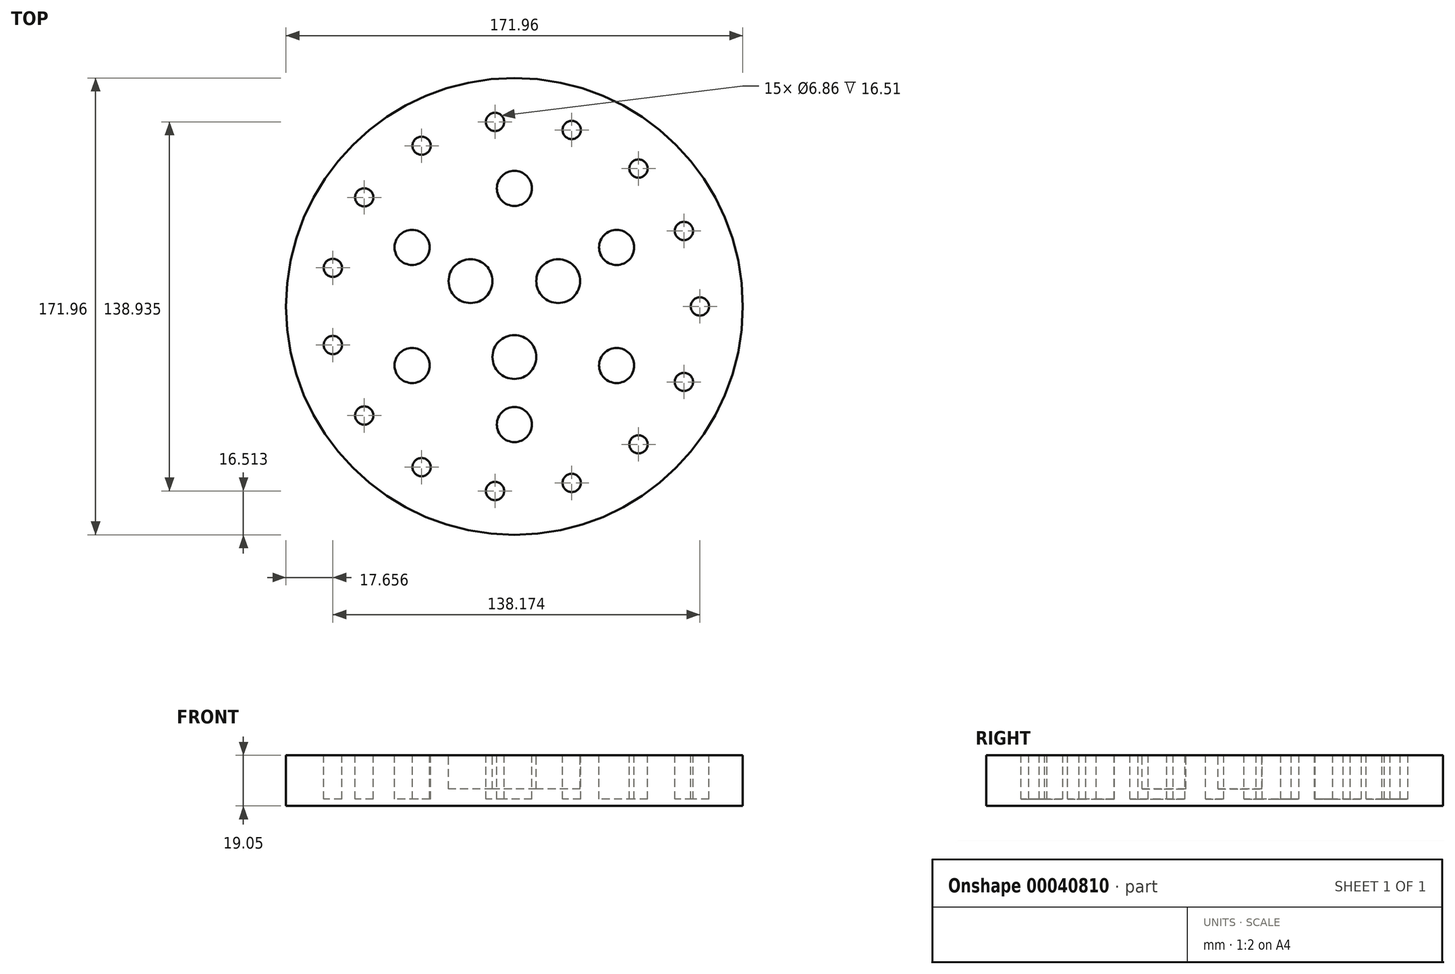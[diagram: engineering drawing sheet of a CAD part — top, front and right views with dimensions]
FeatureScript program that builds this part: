
annotation { "Feature Type Name" : "Feature", "Feature Type Description" : "" }
export const myFeature = defineFeature(function(context is Context, id is Id, definition is map)
    precondition{}
    {
        {
            var Q0;
            Q0=qCreatedBy(makeId("Top.planeOp"),FACE);
            var sketch = newSketch(context, id + "F0", { "sketchPlane" : qUnion([Q0])});
            skCircle(sketch, "E0", {"center": v(0, -19.05) * mm, "radius": 8.26 * mm});
            skCircle(sketch, "E1.1.0", {"center": v(16.5, 9.52) * mm, "radius": 8.26 * mm});
            skCircle(sketch, "E1.2.0", {"center": v(-16.5, 9.52) * mm, "radius": 8.26 * mm});
            skPoint(sketch, "E1.center", {"position": v(0, 0) * mm});
            skCircle(sketch, "E2", {"center": v(0, 44.45) * mm, "radius": 6.6 * mm});
            skCircle(sketch, "E3.1.0", {"center": v(-38.5, 22.23) * mm, "radius": 6.6 * mm});
            skCircle(sketch, "E3.2.0", {"center": v(-38.5, -22.23) * mm, "radius": 6.6 * mm});
            skCircle(sketch, "E4.1.3.0", {"center": v(0, -44.45) * mm, "radius": 6.6 * mm});
            skCircle(sketch, "E4.1.4.0", {"center": v(38.5, -22.23) * mm, "radius": 6.6 * mm});
            skCircle(sketch, "E4.1.5.0", {"center": v(38.5, 22.23) * mm, "radius": 6.6 * mm});
            skCircle(sketch, "E5", {"center": v(69.85, 0) * mm, "radius": 3.43 * mm});
            skCircle(sketch, "E6.1.0", {"center": v(63.81, 28.41) * mm, "radius": 3.43 * mm});
            skCircle(sketch, "E6.2.0", {"center": v(46.74, 51.9) * mm, "radius": 3.43 * mm});
            skCircle(sketch, "E6.3.0", {"center": v(21.58, 66.43) * mm, "radius": 3.43 * mm});
            skCircle(sketch, "E6.4.0", {"center": v(-7.3, 69.47) * mm, "radius": 3.43 * mm});
            skCircle(sketch, "E6.5.0", {"center": v(-34.92, 60.5) * mm, "radius": 3.43 * mm});
            skCircle(sketch, "E6.6.0", {"center": v(-56.5, 41.06) * mm, "radius": 3.43 * mm});
            skCircle(sketch, "E6.7.0", {"center": v(-68.32, 14.52) * mm, "radius": 3.43 * mm});
            skCircle(sketch, "E6.8.0", {"center": v(-68.32, -14.52) * mm, "radius": 3.43 * mm});
            skCircle(sketch, "E6.9.0", {"center": v(-56.5, -41.06) * mm, "radius": 3.43 * mm});
            skCircle(sketch, "E6.10.0", {"center": v(-34.93, -60.5) * mm, "radius": 3.43 * mm});
            skCircle(sketch, "E6.11.0", {"center": v(-7.3, -69.47) * mm, "radius": 3.43 * mm});
            skCircle(sketch, "E6.12.0", {"center": v(21.58, -66.43) * mm, "radius": 3.43 * mm});
            skCircle(sketch, "E6.13.0", {"center": v(46.74, -51.9) * mm, "radius": 3.43 * mm});
            skCircle(sketch, "E6.14.0", {"center": v(63.81, -28.41) * mm, "radius": 3.43 * mm});
            skCircle(sketch, "E7", {"center": v(0, 0) * mm, "radius": 85.98 * mm});
            skSolve(sketch);
        }
        {
            var Q0;
            Q0=makeQuery(id+"F0.imprint","IMPRINT",FACE,{"disambiguationData":[TD([[makeQuery(id+"F0.imprint","IMPRINT",EDGE,{"derivedFrom":sQuery(id+"F0.wireOp",EDGE,"E0")}),-1.0]])]});
            var Q1;
            Q1=makeQuery(id+"F0.imprint","IMPRINT",FACE,{"disambiguationData":[TD([[makeQuery(id+"F0.imprint","IMPRINT",EDGE,{"derivedFrom":sQuery(id+"F0.wireOp",EDGE,"E6.7.0")}),1.0]])]});
            var Q2;
            Q2=makeQuery(id+"F0.imprint","IMPRINT",FACE,{"disambiguationData":[TD([[makeQuery(id+"F0.imprint","IMPRINT",EDGE,{"derivedFrom":sQuery(id+"F0.wireOp",EDGE,"E6.8.0")}),1.0]])]});
            var Q3;
            Q3=makeQuery(id+"F0.imprint","IMPRINT",FACE,{"disambiguationData":[TD([[makeQuery(id+"F0.imprint","IMPRINT",EDGE,{"derivedFrom":sQuery(id+"F0.wireOp",EDGE,"E6.9.0")}),1.0]])]});
            var Q4;
            Q4=makeQuery(id+"F0.imprint","IMPRINT",FACE,{"disambiguationData":[TD([[makeQuery(id+"F0.imprint","IMPRINT",EDGE,{"derivedFrom":sQuery(id+"F0.wireOp",EDGE,"E6.10.0")}),1.0]])]});
            var Q5;
            Q5=makeQuery(id+"F0.imprint","IMPRINT",FACE,{"disambiguationData":[TD([[makeQuery(id+"F0.imprint","IMPRINT",EDGE,{"derivedFrom":sQuery(id+"F0.wireOp",EDGE,"E6.11.0")}),1.0]])]});
            var Q6;
            Q6=makeQuery(id+"F0.imprint","IMPRINT",FACE,{"disambiguationData":[TD([[makeQuery(id+"F0.imprint","IMPRINT",EDGE,{"derivedFrom":sQuery(id+"F0.wireOp",EDGE,"E6.12.0")}),1.0]])]});
            var Q7;
            Q7=makeQuery(id+"F0.imprint","IMPRINT",FACE,{"disambiguationData":[TD([[makeQuery(id+"F0.imprint","IMPRINT",EDGE,{"derivedFrom":sQuery(id+"F0.wireOp",EDGE,"E6.13.0")}),1.0]])]});
            var Q8;
            Q8=makeQuery(id+"F0.imprint","IMPRINT",FACE,{"disambiguationData":[TD([[makeQuery(id+"F0.imprint","IMPRINT",EDGE,{"derivedFrom":sQuery(id+"F0.wireOp",EDGE,"E6.14.0")}),1.0]])]});
            var Q9;
            Q9=makeQuery(id+"F0.imprint","IMPRINT",FACE,{"disambiguationData":[TD([[makeQuery(id+"F0.imprint","IMPRINT",EDGE,{"derivedFrom":sQuery(id+"F0.wireOp",EDGE,"E5")}),1.0]])]});
            var Q10;
            Q10=makeQuery(id+"F0.imprint","IMPRINT",FACE,{"disambiguationData":[TD([[makeQuery(id+"F0.imprint","IMPRINT",EDGE,{"derivedFrom":sQuery(id+"F0.wireOp",EDGE,"E6.1.0")}),1.0]])]});
            var Q11;
            Q11=makeQuery(id+"F0.imprint","IMPRINT",FACE,{"disambiguationData":[TD([[makeQuery(id+"F0.imprint","IMPRINT",EDGE,{"derivedFrom":sQuery(id+"F0.wireOp",EDGE,"E6.2.0")}),1.0]])]});
            var Q12;
            Q12=makeQuery(id+"F0.imprint","IMPRINT",FACE,{"disambiguationData":[TD([[makeQuery(id+"F0.imprint","IMPRINT",EDGE,{"derivedFrom":sQuery(id+"F0.wireOp",EDGE,"E6.3.0")}),1.0]])]});
            var Q13;
            Q13=makeQuery(id+"F0.imprint","IMPRINT",FACE,{"disambiguationData":[TD([[makeQuery(id+"F0.imprint","IMPRINT",EDGE,{"derivedFrom":sQuery(id+"F0.wireOp",EDGE,"E6.4.0")}),1.0]])]});
            var Q14;
            Q14=makeQuery(id+"F0.imprint","IMPRINT",FACE,{"disambiguationData":[TD([[makeQuery(id+"F0.imprint","IMPRINT",EDGE,{"derivedFrom":sQuery(id+"F0.wireOp",EDGE,"E6.5.0")}),1.0]])]});
            var Q15;
            Q15=makeQuery(id+"F0.imprint","IMPRINT",FACE,{"disambiguationData":[TD([[makeQuery(id+"F0.imprint","IMPRINT",EDGE,{"derivedFrom":sQuery(id+"F0.wireOp",EDGE,"E6.6.0")}),1.0]])]});
            var Q16;
            Q16=makeQuery(id+"F0.imprint","IMPRINT",FACE,{"disambiguationData":[TD([[makeQuery(id+"F0.imprint","IMPRINT",EDGE,{"derivedFrom":sQuery(id+"F0.wireOp",EDGE,"E3.1.0")}),1.0]])]});
            var Q17;
            Q17=makeQuery(id+"F0.imprint","IMPRINT",FACE,{"disambiguationData":[TD([[makeQuery(id+"F0.imprint","IMPRINT",EDGE,{"derivedFrom":sQuery(id+"F0.wireOp",EDGE,"E3.2.0")}),1.0]])]});
            var Q18;
            Q18=makeQuery(id+"F0.imprint","IMPRINT",FACE,{"disambiguationData":[TD([[makeQuery(id+"F0.imprint","IMPRINT",EDGE,{"derivedFrom":sQuery(id+"F0.wireOp",EDGE,"E4.1.3.0")}),1.0]])]});
            var Q19;
            Q19=makeQuery(id+"F0.imprint","IMPRINT",FACE,{"disambiguationData":[TD([[makeQuery(id+"F0.imprint","IMPRINT",EDGE,{"derivedFrom":sQuery(id+"F0.wireOp",EDGE,"E0")}),1.0]])]});
            var Q20;
            Q20=makeQuery(id+"F0.imprint","IMPRINT",FACE,{"disambiguationData":[TD([[makeQuery(id+"F0.imprint","IMPRINT",EDGE,{"derivedFrom":sQuery(id+"F0.wireOp",EDGE,"E1.2.0")}),1.0]])]});
            var Q21;
            Q21=makeQuery(id+"F0.imprint","IMPRINT",FACE,{"disambiguationData":[TD([[makeQuery(id+"F0.imprint","IMPRINT",EDGE,{"derivedFrom":sQuery(id+"F0.wireOp",EDGE,"E1.1.0")}),1.0]])]});
            var Q22;
            Q22=makeQuery(id+"F0.imprint","IMPRINT",FACE,{"disambiguationData":[TD([[makeQuery(id+"F0.imprint","IMPRINT",EDGE,{"derivedFrom":sQuery(id+"F0.wireOp",EDGE,"E4.1.4.0")}),1.0]])]});
            var Q23;
            Q23=makeQuery(id+"F0.imprint","IMPRINT",FACE,{"disambiguationData":[TD([[makeQuery(id+"F0.imprint","IMPRINT",EDGE,{"derivedFrom":sQuery(id+"F0.wireOp",EDGE,"E4.1.5.0")}),1.0]])]});
            var Q24;
            Q24=makeQuery(id+"F0.imprint","IMPRINT",FACE,{"disambiguationData":[TD([[makeQuery(id+"F0.imprint","IMPRINT",EDGE,{"derivedFrom":sQuery(id+"F0.wireOp",EDGE,"E2")}),1.0]])]});
            extrude(context, id + "F1", {"entities" : qUnion([Q0, Q1, Q2, Q3, Q4, Q5, Q6, Q7, Q8, Q9, Q10, Q11, Q12, Q13, Q14, Q15, Q16, Q17, Q18, Q19, Q20, Q21, Q22, Q23, Q24]), "oppositeDirection" : true, "depth" : 19.05 * mm});
        }
        {
            var Q0;
            Q0=makeQuery(id+"F0.imprint","IMPRINT",FACE,{"disambiguationData":[TD([[makeQuery(id+"F0.imprint","IMPRINT",EDGE,{"derivedFrom":sQuery(id+"F0.wireOp",EDGE,"E6.7.0")}),1.0]])]});
            var Q1;
            Q1=makeQuery(id+"F0.imprint","IMPRINT",FACE,{"disambiguationData":[TD([[makeQuery(id+"F0.imprint","IMPRINT",EDGE,{"derivedFrom":sQuery(id+"F0.wireOp",EDGE,"E6.8.0")}),1.0]])]});
            var Q2;
            Q2=makeQuery(id+"F0.imprint","IMPRINT",FACE,{"disambiguationData":[TD([[makeQuery(id+"F0.imprint","IMPRINT",EDGE,{"derivedFrom":sQuery(id+"F0.wireOp",EDGE,"E6.9.0")}),1.0]])]});
            var Q3;
            Q3=makeQuery(id+"F0.imprint","IMPRINT",FACE,{"disambiguationData":[TD([[makeQuery(id+"F0.imprint","IMPRINT",EDGE,{"derivedFrom":sQuery(id+"F0.wireOp",EDGE,"E6.10.0")}),1.0]])]});
            var Q4;
            Q4=makeQuery(id+"F0.imprint","IMPRINT",FACE,{"disambiguationData":[TD([[makeQuery(id+"F0.imprint","IMPRINT",EDGE,{"derivedFrom":sQuery(id+"F0.wireOp",EDGE,"E6.11.0")}),1.0]])]});
            var Q5;
            Q5=makeQuery(id+"F0.imprint","IMPRINT",FACE,{"disambiguationData":[TD([[makeQuery(id+"F0.imprint","IMPRINT",EDGE,{"derivedFrom":sQuery(id+"F0.wireOp",EDGE,"E6.12.0")}),1.0]])]});
            var Q6;
            Q6=makeQuery(id+"F0.imprint","IMPRINT",FACE,{"disambiguationData":[TD([[makeQuery(id+"F0.imprint","IMPRINT",EDGE,{"derivedFrom":sQuery(id+"F0.wireOp",EDGE,"E6.13.0")}),1.0]])]});
            var Q7;
            Q7=makeQuery(id+"F0.imprint","IMPRINT",FACE,{"disambiguationData":[TD([[makeQuery(id+"F0.imprint","IMPRINT",EDGE,{"derivedFrom":sQuery(id+"F0.wireOp",EDGE,"E6.14.0")}),1.0]])]});
            var Q8;
            Q8=makeQuery(id+"F0.imprint","IMPRINT",FACE,{"disambiguationData":[TD([[makeQuery(id+"F0.imprint","IMPRINT",EDGE,{"derivedFrom":sQuery(id+"F0.wireOp",EDGE,"E5")}),1.0]])]});
            var Q9;
            Q9=makeQuery(id+"F0.imprint","IMPRINT",FACE,{"disambiguationData":[TD([[makeQuery(id+"F0.imprint","IMPRINT",EDGE,{"derivedFrom":sQuery(id+"F0.wireOp",EDGE,"E6.1.0")}),1.0]])]});
            var Q10;
            Q10=makeQuery(id+"F0.imprint","IMPRINT",FACE,{"disambiguationData":[TD([[makeQuery(id+"F0.imprint","IMPRINT",EDGE,{"derivedFrom":sQuery(id+"F0.wireOp",EDGE,"E6.2.0")}),1.0]])]});
            var Q11;
            Q11=makeQuery(id+"F0.imprint","IMPRINT",FACE,{"disambiguationData":[TD([[makeQuery(id+"F0.imprint","IMPRINT",EDGE,{"derivedFrom":sQuery(id+"F0.wireOp",EDGE,"E6.3.0")}),1.0]])]});
            var Q12;
            Q12=makeQuery(id+"F0.imprint","IMPRINT",FACE,{"disambiguationData":[TD([[makeQuery(id+"F0.imprint","IMPRINT",EDGE,{"derivedFrom":sQuery(id+"F0.wireOp",EDGE,"E6.4.0")}),1.0]])]});
            var Q13;
            Q13=makeQuery(id+"F0.imprint","IMPRINT",FACE,{"disambiguationData":[TD([[makeQuery(id+"F0.imprint","IMPRINT",EDGE,{"derivedFrom":sQuery(id+"F0.wireOp",EDGE,"E6.5.0")}),1.0]])]});
            var Q14;
            Q14=makeQuery(id+"F0.imprint","IMPRINT",FACE,{"disambiguationData":[TD([[makeQuery(id+"F0.imprint","IMPRINT",EDGE,{"derivedFrom":sQuery(id+"F0.wireOp",EDGE,"E6.6.0")}),1.0]])]});
            var Q15;
            Q15=makeQuery(id+"F0.imprint","IMPRINT",FACE,{"disambiguationData":[TD([[makeQuery(id+"F0.imprint","IMPRINT",EDGE,{"derivedFrom":sQuery(id+"F0.wireOp",EDGE,"E3.2.0")}),1.0]])]});
            var Q16;
            Q16=makeQuery(id+"F0.imprint","IMPRINT",FACE,{"disambiguationData":[TD([[makeQuery(id+"F0.imprint","IMPRINT",EDGE,{"derivedFrom":sQuery(id+"F0.wireOp",EDGE,"E4.1.3.0")}),1.0]])]});
            var Q17;
            Q17=makeQuery(id+"F0.imprint","IMPRINT",FACE,{"disambiguationData":[TD([[makeQuery(id+"F0.imprint","IMPRINT",EDGE,{"derivedFrom":sQuery(id+"F0.wireOp",EDGE,"E4.1.4.0")}),1.0]])]});
            var Q18;
            Q18=makeQuery(id+"F0.imprint","IMPRINT",FACE,{"disambiguationData":[TD([[makeQuery(id+"F0.imprint","IMPRINT",EDGE,{"derivedFrom":sQuery(id+"F0.wireOp",EDGE,"E4.1.5.0")}),1.0]])]});
            var Q19;
            Q19=makeQuery(id+"F0.imprint","IMPRINT",FACE,{"disambiguationData":[TD([[makeQuery(id+"F0.imprint","IMPRINT",EDGE,{"derivedFrom":sQuery(id+"F0.wireOp",EDGE,"E2")}),1.0]])]});
            var Q20;
            Q20=makeQuery(id+"F0.imprint","IMPRINT",FACE,{"disambiguationData":[TD([[makeQuery(id+"F0.imprint","IMPRINT",EDGE,{"derivedFrom":sQuery(id+"F0.wireOp",EDGE,"E3.1.0")}),1.0]])]});
            extrude(context, id + "F2", {"entities" : qUnion([Q0, Q1, Q2, Q3, Q4, Q5, Q6, Q7, Q8, Q9, Q10, Q11, Q12, Q13, Q14, Q15, Q16, Q17, Q18, Q19, Q20]), "operationType" : NewBodyOperationType.REMOVE, "oppositeDirection" : true, "depth" : 16.5 * mm});
        }
        {
            var Q0;
            Q0=makeQuery(id+"F0.imprint","IMPRINT",FACE,{"disambiguationData":[TD([[makeQuery(id+"F0.imprint","IMPRINT",EDGE,{"derivedFrom":sQuery(id+"F0.wireOp",EDGE,"E1.2.0")}),1.0]])]});
            var Q1;
            Q1=makeQuery(id+"F0.imprint","IMPRINT",FACE,{"disambiguationData":[TD([[makeQuery(id+"F0.imprint","IMPRINT",EDGE,{"derivedFrom":sQuery(id+"F0.wireOp",EDGE,"E0")}),1.0]])]});
            var Q2;
            Q2=makeQuery(id+"F0.imprint","IMPRINT",FACE,{"disambiguationData":[TD([[makeQuery(id+"F0.imprint","IMPRINT",EDGE,{"derivedFrom":sQuery(id+"F0.wireOp",EDGE,"E1.1.0")}),1.0]])]});
            extrude(context, id + "F3", {"entities" : qUnion([Q0, Q1, Q2]), "operationType" : NewBodyOperationType.REMOVE, "oppositeDirection" : true, "depth" : 12.7 * mm});
        }
    });
